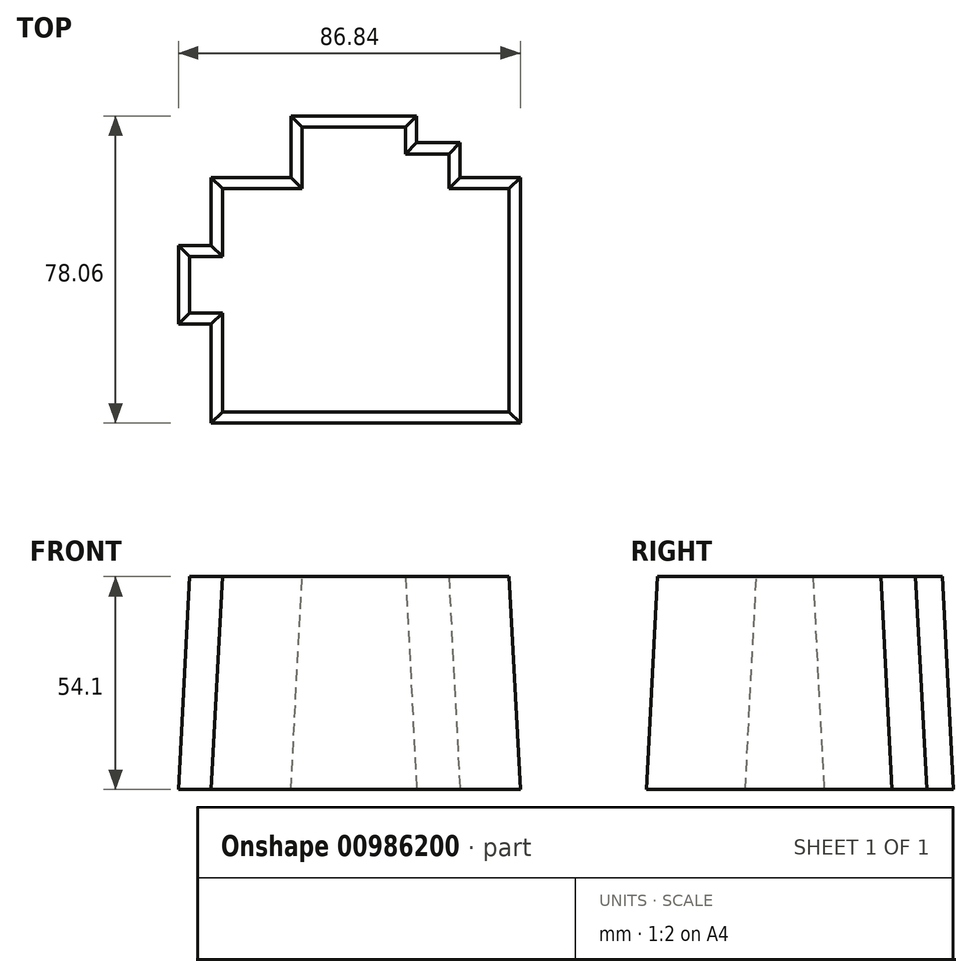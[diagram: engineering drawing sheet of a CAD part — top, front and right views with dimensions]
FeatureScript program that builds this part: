
annotation { "Feature Type Name" : "Feature", "Feature Type Description" : "" }
export const myFeature = defineFeature(function(context is Context, id is Id, definition is map)
    precondition{}
    {
        {
            var Q0;
            Q0=qCreatedBy(makeId("Top.planeOp"),FACE);
            var sketch = newSketch(context, id + "F0", { "sketchPlane" : qUnion([Q0])});
            skLineSegment(sketch, "E0.bottom", {"start": v(-35.32, 23.47) * mm, "end": v(-15.08, 23.47) * mm});
            skLineSegment(sketch, "E0.top", {"start": v(-35.32, -38.98) * mm, "end": v(43.22, -38.98) * mm});
            skLineSegment(sketch, "E0.left", {"start": v(-35.32, 23.47) * mm, "end": v(-35.32, 6.15) * mm});
            skLineSegment(sketch, "E0.right", {"start": v(43.22, 23.47) * mm, "end": v(43.22, -38.98) * mm});
            skPoint(sketch, "E1.firstSnap0", {"position": v(3.95, 23.47) * mm});
            skLineSegment(sketch, "E1.bottom", {"start": v(16.88, 32.25) * mm, "end": v(27.86, 32.25) * mm});
            skLineSegment(sketch, "E1.right", {"start": v(27.86, 32.25) * mm, "end": v(27.86, 23.47) * mm});
            skLineSegment(sketch, "E2.bottom", {"start": v(16.88, 39.08) * mm, "end": v(-15.08, 39.08) * mm});
            skLineSegment(sketch, "E2.left", {"start": v(16.88, 39.08) * mm, "end": v(16.88, 32.25) * mm});
            skLineSegment(sketch, "E2.right", {"start": v(-15.08, 39.08) * mm, "end": v(-15.08, 23.47) * mm});
            skLineSegment(sketch, "E3.bottom", {"start": v(-35.32, 6.15) * mm, "end": v(-43.62, 6.15) * mm});
            skLineSegment(sketch, "E3.top", {"start": v(-35.32, -13.86) * mm, "end": v(-43.62, -13.86) * mm});
            skLineSegment(sketch, "E3.right", {"start": v(-43.62, 6.15) * mm, "end": v(-43.62, -13.86) * mm});
            skLineSegment(sketch, "E4.trimOffspring", {"start": v(-35.32, -13.86) * mm, "end": v(-35.32, -38.98) * mm});
            skLineSegment(sketch, "E5.trimOffspring", {"start": v(27.86, 23.47) * mm, "end": v(43.22, 23.47) * mm});
            skPoint(sketch, "E6.orphan", {"position": v(3.95, 32.25) * mm});
            skSolve(sketch);
        }
        {
            var Q0;
            Q0 = qSketchRegion(id + "F0", true);
            extrude(context, id + "F1", {"entities" : qUnion([Q0]), "depth" : 54.1 * mm, "offsetDistance" : 25.4 * mm, "hasDraft" : true, "draftAngle" : 3 * degree, "draftPullDirection" : true});
        }
    });
